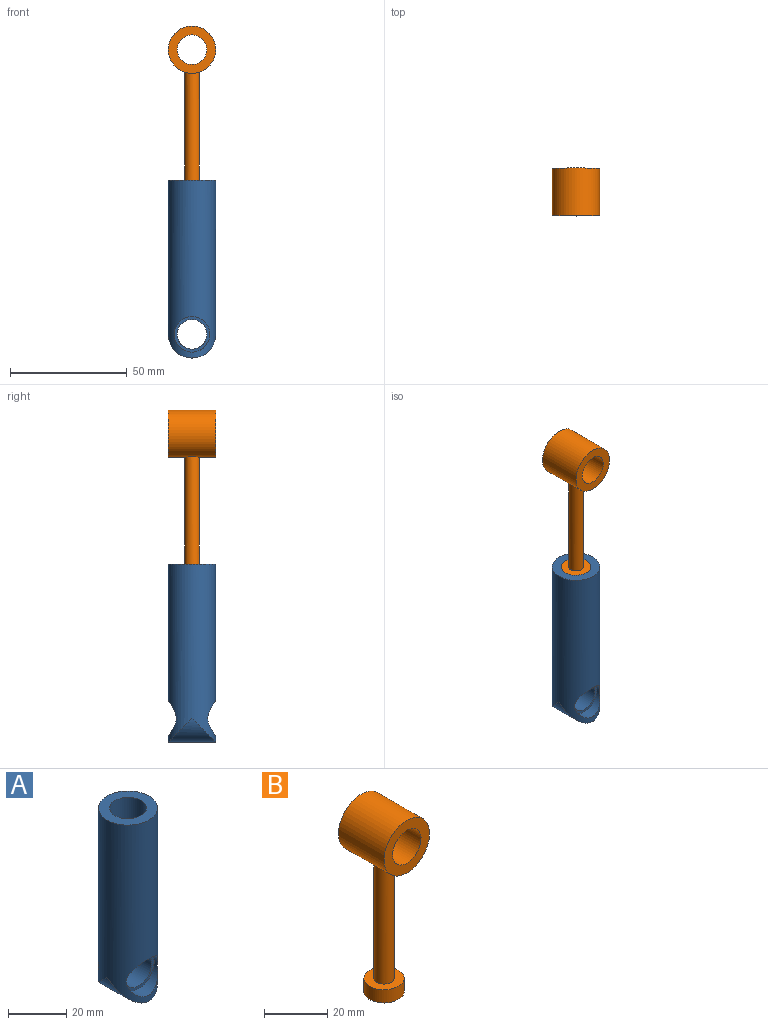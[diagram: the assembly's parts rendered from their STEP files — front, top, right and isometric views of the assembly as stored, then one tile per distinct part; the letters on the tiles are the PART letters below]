
ASSEMBLY  parts=2 mates=1
PART A: 10 faces, bbox 20.3x20.4x76.2 mm
  f0: cylinder r=10.16mm len=20.39mm, axis (0,1,0), area 412.9mm2, adj f5
  f1: cylinder r=7.62mm len=15.24mm, axis (0,-1,0), area 165.1mm2, adj f5,f9
  f2: cylinder r=6.35mm len=12.7mm, axis (0,1,0), area 405.4mm2, adj f8,f9
  f3: cylinder r=7.62mm len=15.24mm, axis (0,1,0), area 165.1mm2, adj f5,f8
  f4: cylinder r=6.35mm len=50.8mm, axis (0,0,-1), area 2026.8mm2, adj f6,f7
  f5: cylinder r=10.16mm len=76.23mm, axis (0,0,-1), area 4230.4mm2, adj f0,f1,f3,f6
  f6: plane 20.32x20.32mm, normal (0,0,1), area 197.6mm2, adj f4,f5
  f7: plane 12.7x12.7mm, normal (0,0,1), area 126.7mm2, adj f4
  f8: plane 15.24x15.24mm, normal (0,1,0), area 55.7mm2, adj f2,f3
  f9: plane 15.24x15.24mm, normal (0,-1,0), area 55.7mm2, adj f1,f2
PART B: 8 faces, bbox 20.3x20.3x71.1 mm
  f0: cylinder r=6.35mm len=12.7mm, axis (0,0,-1), area 202.7mm2, adj f1,f2
  f1: plane 12.7x12.7mm, normal (0,0,1), area 95mm2, adj f0,f3
  f2: plane 12.7x12.7mm, normal (0,0,-1), area 126.7mm2, adj f0
  f3: cylinder r=3.17mm len=46.23mm, axis (0,0,-1), area 917.1mm2, adj f1,f7
  f4: plane 20.32x20.32mm, normal (0,-1,0), area 197.6mm2, adj f6,f7
  f5: plane 20.32x20.32mm, normal (0,1,0), area 197.6mm2, adj f6,f7
  f6: cylinder r=6.35mm len=20.32mm, axis (0,-1,0), area 810.7mm2, adj f4,f5
  f7: cylinder r=10.16mm len=20.32mm, axis (0,1,0), area 1265.1mm2, adj f3,f4,f5
PLACE A t=(-63.54,-7.29,-1.41)mm
PLACE B t=(-2.87,57.93,44.31)mm
MATE slider B.f0 <-> A.f4  axis (0,0,-1) through (-63.54,-7.29,44.31)mm
